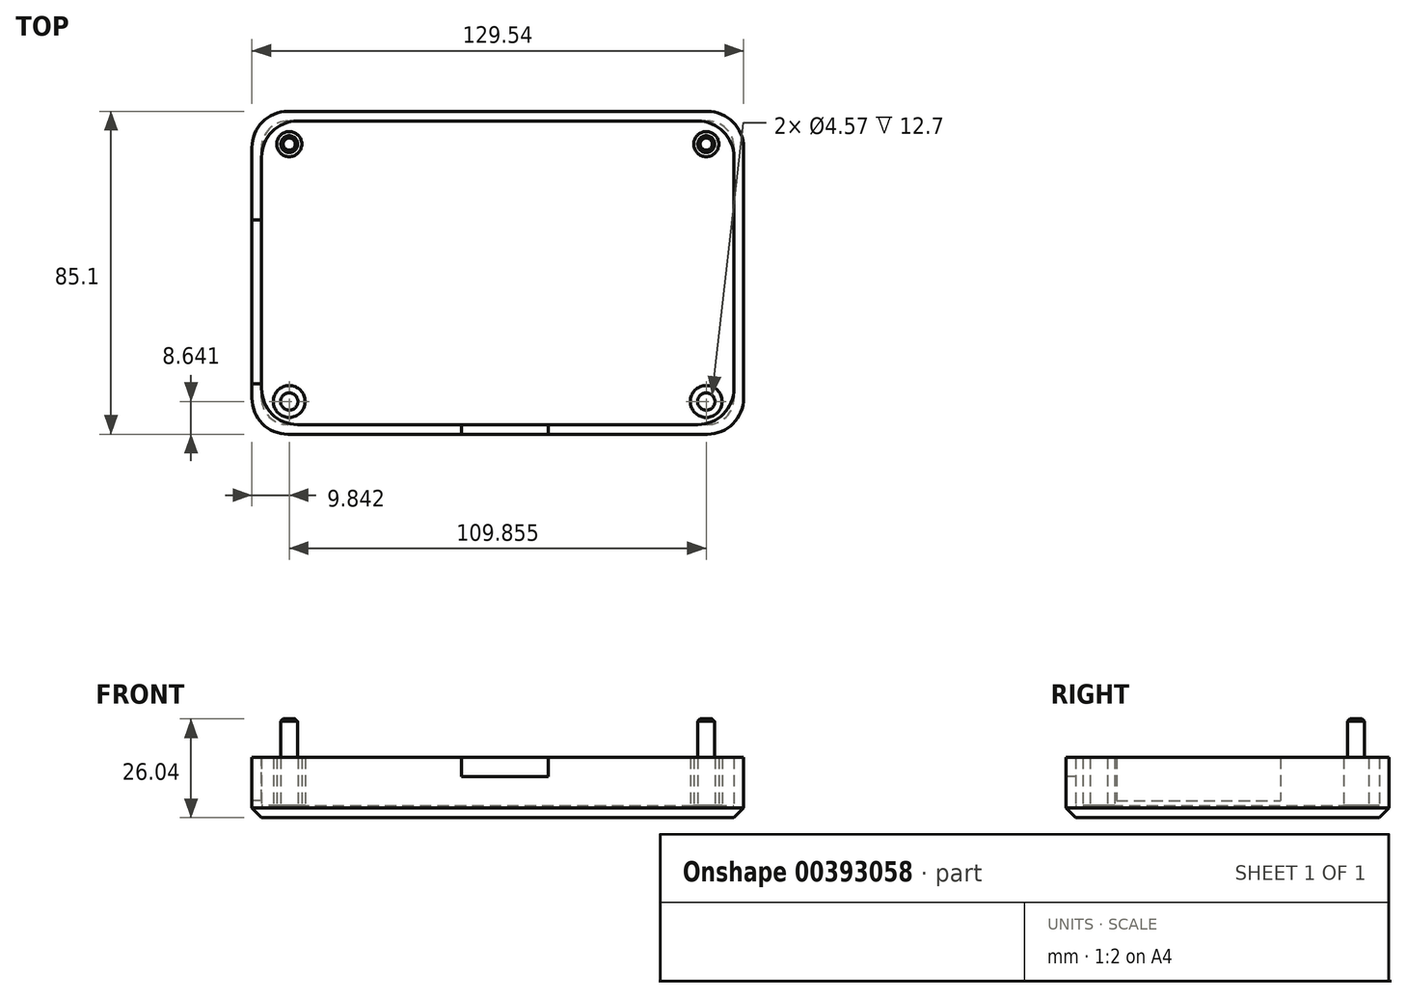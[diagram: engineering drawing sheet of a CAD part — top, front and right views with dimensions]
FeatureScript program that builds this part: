
annotation { "Feature Type Name" : "Feature", "Feature Type Description" : "" }
export const myFeature = defineFeature(function(context is Context, id is Id, definition is map)
    precondition{}
    {
        {
            var Q0;
            Q0=qCreatedBy(makeId("Top.planeOp"),FACE);
            var sketch = newSketch(context, id + "F0", { "sketchPlane" : qUnion([Q0])});
            skLineSegment(sketch, "E0.bottom", {"start": v(64.77, -42.55) * mm, "end": v(-64.77, -42.55) * mm});
            skLineSegment(sketch, "E0.top", {"start": v(64.77, 42.55) * mm, "end": v(-64.77, 42.55) * mm});
            skLineSegment(sketch, "E0.left", {"start": v(64.77, -42.55) * mm, "end": v(64.77, 42.55) * mm});
            skLineSegment(sketch, "E0.right", {"start": v(-64.77, -42.55) * mm, "end": v(-64.77, 42.55) * mm});
            skPoint(sketch, "E0.middle", {"position": v(0, 0) * mm});
            skSolve(sketch);
        }
        {
            var Q0;
            Q0=makeQuery(id+"F0.imprint","IMPRINT",FACE,{"disambiguationData":[TD([[makeQuery(id+"F0.imprint","IMPRINT",EDGE,{"derivedFrom":sQuery(id+"F0.wireOp",EDGE,"E0.bottom")}),-1.0]])]});
            extrude(context, id + "F1", {"entities" : qUnion([Q0]), "depth" : 3.17 * mm});
        }
        {
            var Q0;
            Q0=makeQuery(id+"F1.opExtrude","CAP_FACE",FACE,{"disambiguationData":[OSD([sQuery(id+"F0.wireOp",EDGE,"E0.bottom"),sQuery(id+"F0.wireOp",EDGE,"E0.top"),sQuery(id+"F0.wireOp",EDGE,"E0.left"),sQuery(id+"F0.wireOp",EDGE,"E0.right")])],"isStart":false});
            var sketch = newSketch(context, id + "F2", { "sketchPlane" : qUnion([Q0])});
            skLineSegment(sketch, "E1.bottom", {"start": v(-62.23, -40) * mm, "end": v(62.23, -40) * mm});
            skLineSegment(sketch, "E1.top", {"start": v(-62.23, 40) * mm, "end": v(62.23, 40) * mm});
            skLineSegment(sketch, "E1.left", {"start": v(-62.23, -40) * mm, "end": v(-62.23, 40) * mm});
            skLineSegment(sketch, "E1.right", {"start": v(62.23, -40) * mm, "end": v(62.23, 40) * mm});
            skPoint(sketch, "E1.middle", {"position": v(0, 0) * mm});
            skPoint(sketch, "E2", {"position": v(-54.93, 33.9) * mm});
            skPoint(sketch, "E3", {"position": v(54.93, 33.9) * mm});
            skPoint(sketch, "E4", {"position": v(54.93, -33.9) * mm});
            skPoint(sketch, "E5", {"position": v(-54.93, -33.9) * mm});
            skCircle(sketch, "E6", {"center": v(-54.93, -33.9) * mm, "radius": 2.29 * mm});
            skCircle(sketch, "E7", {"center": v(-54.93, -33.9) * mm, "radius": 4.2 * mm});
            skCircle(sketch, "E8", {"center": v(54.93, -33.9) * mm, "radius": 2.29 * mm});
            skCircle(sketch, "E9", {"center": v(54.93, -33.9) * mm, "radius": 4.2 * mm});
            skCircle(sketch, "E10", {"center": v(-54.93, 33.9) * mm, "radius": 3.3 * mm});
            skCircle(sketch, "E11", {"center": v(54.93, 33.9) * mm, "radius": 3.3 * mm});
            skSolve(sketch);
        }
        {
            var Q0;
            Q0=makeQuery(id+"F2.imprint","IMPRINT",FACE,{"disambiguationData":[TD([[makeQuery(id+"F2.imprint","IMPRINT",EDGE,{"derivedFrom":sQuery(id+"F2.wireOp",EDGE,"E1.bottom")}),-1.0]])]});
            extrude(context, id + "F3", {"entities" : qUnion([Q0]), "operationType" : NewBodyOperationType.ADD, "depth" : 12.7 * mm});
        }
        {
            var Q0;
            Q0=makeQuery(id+"F3.opExtrude","SWEPT_EDGE",EDGE,{"disambiguationData":[OSD([sQuery(id+"F2.wireOp",EDGE,"E1.top"),sQuery(id+"F2.wireOp",EDGE,"E1.right")])]});
            var Q1;
            Q1=makeQuery(id+"F3.opExtrude","SWEPT_EDGE",EDGE,{"disambiguationData":[OSD([sQuery(id+"F2.wireOp",EDGE,"E1.bottom"),sQuery(id+"F2.wireOp",EDGE,"E1.right")])]});
            var Q2;
            Q2=makeQuery(id+"F3.opExtrude","SWEPT_EDGE",EDGE,{"disambiguationData":[OSD([sQuery(id+"F2.wireOp",EDGE,"E1.bottom"),sQuery(id+"F2.wireOp",EDGE,"E1.left")])]});
            var Q3;
            Q3=makeQuery(id+"F3.opExtrude","SWEPT_EDGE",EDGE,{"disambiguationData":[OSD([sQuery(id+"F2.wireOp",EDGE,"E1.top"),sQuery(id+"F2.wireOp",EDGE,"E1.left")])]});
            var Q4;
            {var subQ0=sQuery(id+"F0.wireOp",EDGE,"E0.left");var subQ1=sQuery(id+"F0.wireOp",EDGE,"E0.top");Q4=makeQuery(id+"F3.boolean.opBoolean","MERGE",EDGE,{"derivedFrom":[makeQuery(id+"F1.opExtrude","SWEPT_EDGE",EDGE,{"disambiguationData":[OSD([subQ1,subQ0])]}),makeQuery(id+"F3.opExtrude","SWEPT_EDGE",EDGE,{"disambiguationData":[OSD([subQ1,subQ0])]})]});}
            var Q5;
            {var subQ0=sQuery(id+"F0.wireOp",EDGE,"E0.left");var subQ1=sQuery(id+"F0.wireOp",EDGE,"E0.bottom");Q5=makeQuery(id+"F3.boolean.opBoolean","MERGE",EDGE,{"derivedFrom":[makeQuery(id+"F1.opExtrude","SWEPT_EDGE",EDGE,{"disambiguationData":[OSD([subQ1,subQ0])]}),makeQuery(id+"F3.opExtrude","SWEPT_EDGE",EDGE,{"disambiguationData":[OSD([subQ1,subQ0])]})]});}
            var Q6;
            {var subQ0=sQuery(id+"F0.wireOp",EDGE,"E0.right");var subQ1=sQuery(id+"F0.wireOp",EDGE,"E0.bottom");Q6=makeQuery(id+"F3.boolean.opBoolean","MERGE",EDGE,{"derivedFrom":[makeQuery(id+"F1.opExtrude","SWEPT_EDGE",EDGE,{"disambiguationData":[OSD([subQ1,subQ0])]}),makeQuery(id+"F3.opExtrude","SWEPT_EDGE",EDGE,{"disambiguationData":[OSD([subQ1,subQ0])]})]});}
            var Q7;
            {var subQ0=sQuery(id+"F0.wireOp",EDGE,"E0.right");var subQ1=sQuery(id+"F0.wireOp",EDGE,"E0.top");Q7=makeQuery(id+"F3.boolean.opBoolean","MERGE",EDGE,{"derivedFrom":[makeQuery(id+"F1.opExtrude","SWEPT_EDGE",EDGE,{"disambiguationData":[OSD([subQ1,subQ0])]}),makeQuery(id+"F3.opExtrude","SWEPT_EDGE",EDGE,{"disambiguationData":[OSD([subQ1,subQ0])]})]});}
            fillet(context, id + "F4", {"entities" : qUnion([Q0, Q1, Q2, Q3, Q4, Q5, Q6, Q7]), "radius" : 9.52 * mm, "tangentPropagation" : true, "allowEdgeOverflow" : false});
        }
        {
            var Q0;
            Q0=makeQuery(id+"F3.opExtrude","CAP_EDGE",EDGE,{"disambiguationData":[OSD([sQuery(id+"F2.wireOp",EDGE,"E1.top")])],"isStart":true});
            var Q1;
            Q1=makeQuery(id+"F1.opExtrude","CAP_EDGE",EDGE,{"disambiguationData":[OSD([sQuery(id+"F0.wireOp",EDGE,"E0.top")])],"isStart":true});
            chamfer(context, id + "F5", {"entities" : qUnion([Q0, Q1]), "width" : 2.54 * mm, "tangentPropagation" : true});
        }
        {
            var Q0;
            Q0=makeQuery(id+"F2.imprint","IMPRINT",FACE,{"disambiguationData":[TD([[makeQuery(id+"F2.imprint","IMPRINT",EDGE,{"derivedFrom":sQuery(id+"F2.wireOp",EDGE,"E6")}),-1.0]])]});
            var Q1;
            Q1=makeQuery(id+"F2.imprint","IMPRINT",FACE,{"disambiguationData":[TD([[makeQuery(id+"F2.imprint","IMPRINT",EDGE,{"derivedFrom":sQuery(id+"F2.wireOp",EDGE,"E8")}),-1.0]])]});
            extrude(context, id + "F6", {"entities" : qUnion([Q0, Q1]), "operationType" : NewBodyOperationType.ADD, "depth" : 12.7 * mm});
        }
        {
            var Q0;
            Q0=makeQuery(id+"F2.imprint","IMPRINT",FACE,{"disambiguationData":[TD([[makeQuery(id+"F2.imprint","IMPRINT",EDGE,{"derivedFrom":sQuery(id+"F2.wireOp",EDGE,"E10")}),1.0]])]});
            var Q1;
            Q1=makeQuery(id+"F2.imprint","IMPRINT",FACE,{"disambiguationData":[TD([[makeQuery(id+"F2.imprint","IMPRINT",EDGE,{"derivedFrom":sQuery(id+"F2.wireOp",EDGE,"E11")}),1.0]])]});
            extrude(context, id + "F7", {"entities" : qUnion([Q0, Q1]), "operationType" : NewBodyOperationType.ADD, "depth" : 12.7 * mm});
        }
        {
            var Q0;
            Q0=makeQuery(id+"F7.opExtrude","CAP_FACE",FACE,{"disambiguationData":[OSD([sQuery(id+"F2.wireOp",EDGE,"E11")])],"isStart":false});
            var sketch = newSketch(context, id + "F8", { "sketchPlane" : qUnion([Q0])});
            skCircle(sketch, "E12", {"center": v(54.93, 33.9) * mm, "radius": 2.22 * mm});
            skSolve(sketch);
        }
        {
            var Q0;
            Q0=makeQuery(id+"F7.opExtrude","CAP_FACE",FACE,{"disambiguationData":[OSD([sQuery(id+"F2.wireOp",EDGE,"E10")])],"isStart":false});
            var sketch = newSketch(context, id + "F9", { "sketchPlane" : qUnion([Q0])});
            skCircle(sketch, "E13", {"center": v(-54.93, 33.9) * mm, "radius": 2.22 * mm});
            skSolve(sketch);
        }
        {
            var Q0;
            Q0=makeQuery(id+"F9.imprint","IMPRINT",FACE,{"disambiguationData":[TD([[makeQuery(id+"F9.imprint","IMPRINT",EDGE,{"derivedFrom":sQuery(id+"F9.wireOp",EDGE,"E13")}),1.0]])]});
            extrude(context, id + "F10", {"entities" : qUnion([Q0]), "operationType" : NewBodyOperationType.ADD, "depth" : 10.16 * mm});
        }
        {
            var Q0;
            Q0=makeQuery(id+"F8.imprint","IMPRINT",FACE,{"disambiguationData":[TD([[makeQuery(id+"F8.imprint","IMPRINT",EDGE,{"derivedFrom":sQuery(id+"F8.wireOp",EDGE,"E12")}),1.0]])]});
            extrude(context, id + "F11", {"entities" : qUnion([Q0]), "operationType" : NewBodyOperationType.ADD, "depth" : 10.16 * mm});
        }
        {
            var Q0;
            {var subQ0=sQuery(id+"F0.wireOp",EDGE,"E0.right");Q0=makeQuery(id+"F3.boolean.opBoolean","MERGE",FACE,{"derivedFrom":[makeQuery(id+"F1.opExtrude","SWEPT_FACE",FACE,{"disambiguationData":[OSD([subQ0])]}),makeQuery(id+"F3.opExtrude","SWEPT_FACE",FACE,{"disambiguationData":[OSD([subQ0])]})]});}
            var sketch = newSketch(context, id + "F12", { "sketchPlane" : qUnion([Q0])});
            skLineSegment(sketch, "E14.bottom", {"start": v(29.21, 15.88) * mm, "end": v(-13.97, 15.88) * mm});
            skLineSegment(sketch, "E14.top", {"start": v(29.21, 4.45) * mm, "end": v(-13.97, 4.44) * mm});
            skLineSegment(sketch, "E14.left", {"start": v(29.21, 15.88) * mm, "end": v(29.21, 4.45) * mm});
            skLineSegment(sketch, "E14.right", {"start": v(-13.97, 15.87) * mm, "end": v(-13.97, 4.44) * mm});
            skSolve(sketch);
        }
        {
            var Q0;
            {var subQ0=sQuery(id+"F0.wireOp",EDGE,"E0.bottom");Q0=makeQuery(id+"F3.boolean.opBoolean","MERGE",FACE,{"derivedFrom":[makeQuery(id+"F1.opExtrude","SWEPT_FACE",FACE,{"disambiguationData":[OSD([subQ0])]}),makeQuery(id+"F3.opExtrude","SWEPT_FACE",FACE,{"disambiguationData":[OSD([subQ0])]})]});}
            var sketch = newSketch(context, id + "F13", { "sketchPlane" : qUnion([Q0])});
            skLineSegment(sketch, "E15", {"start": v(55.25, 15.88) * mm, "end": v(13.33, 15.88) * mm});
            skLineSegment(sketch, "E16.bottom", {"start": v(13.33, 15.88) * mm, "end": v(-9.53, 15.88) * mm});
            skLineSegment(sketch, "E16.top", {"start": v(13.34, 10.8) * mm, "end": v(-9.53, 10.8) * mm});
            skLineSegment(sketch, "E16.left", {"start": v(13.33, 15.88) * mm, "end": v(13.33, 10.8) * mm});
            skLineSegment(sketch, "E16.right", {"start": v(-9.53, 15.88) * mm, "end": v(-9.53, 10.8) * mm});
            skSolve(sketch);
        }
        {
            var Q0;
            Q0=makeQuery(id+"F13.imprint","IMPRINT",FACE,{"disambiguationData":[TD([[makeQuery(id+"F13.imprint","IMPRINT",EDGE,{"derivedFrom":sQuery(id+"F13.wireOp",EDGE,"E16.bottom")}),1.0]])]});
            extrude(context, id + "F14", {"entities" : qUnion([Q0]), "operationType" : NewBodyOperationType.REMOVE, "endBound" : BoundingType.UP_TO_NEXT, "oppositeDirection" : true, "depth" : 25.4 * mm});
        }
        {
            var Q0;
            Q0=makeQuery(id+"F12.imprint","IMPRINT",FACE,{"disambiguationData":[TD([[makeQuery(id+"F12.imprint","IMPRINT",EDGE,{"derivedFrom":sQuery(id+"F12.wireOp",EDGE,"E14.bottom")}),1.0]])]});
            extrude(context, id + "F15", {"entities" : qUnion([Q0]), "operationType" : NewBodyOperationType.REMOVE, "endBound" : BoundingType.UP_TO_NEXT, "oppositeDirection" : true, "depth" : 25.4 * mm});
        }
        {
            var Q0;
            Q0=makeQuery(id+"F10.opExtrude","CAP_EDGE",EDGE,{"disambiguationData":[OSD([sQuery(id+"F9.wireOp",EDGE,"E13")])],"isStart":false});
            chamfer(context, id + "F16", {"entities" : qUnion([Q0]), "width" : 0.64 * mm, "tangentPropagation" : true});
        }
        {
            var Q0;
            Q0=makeQuery(id+"F11.opExtrude","CAP_EDGE",EDGE,{"disambiguationData":[OSD([sQuery(id+"F8.wireOp",EDGE,"E12")])],"isStart":false});
            chamfer(context, id + "F17", {"entities" : qUnion([Q0]), "width" : 0.64 * mm, "tangentPropagation" : true});
        }
    });
